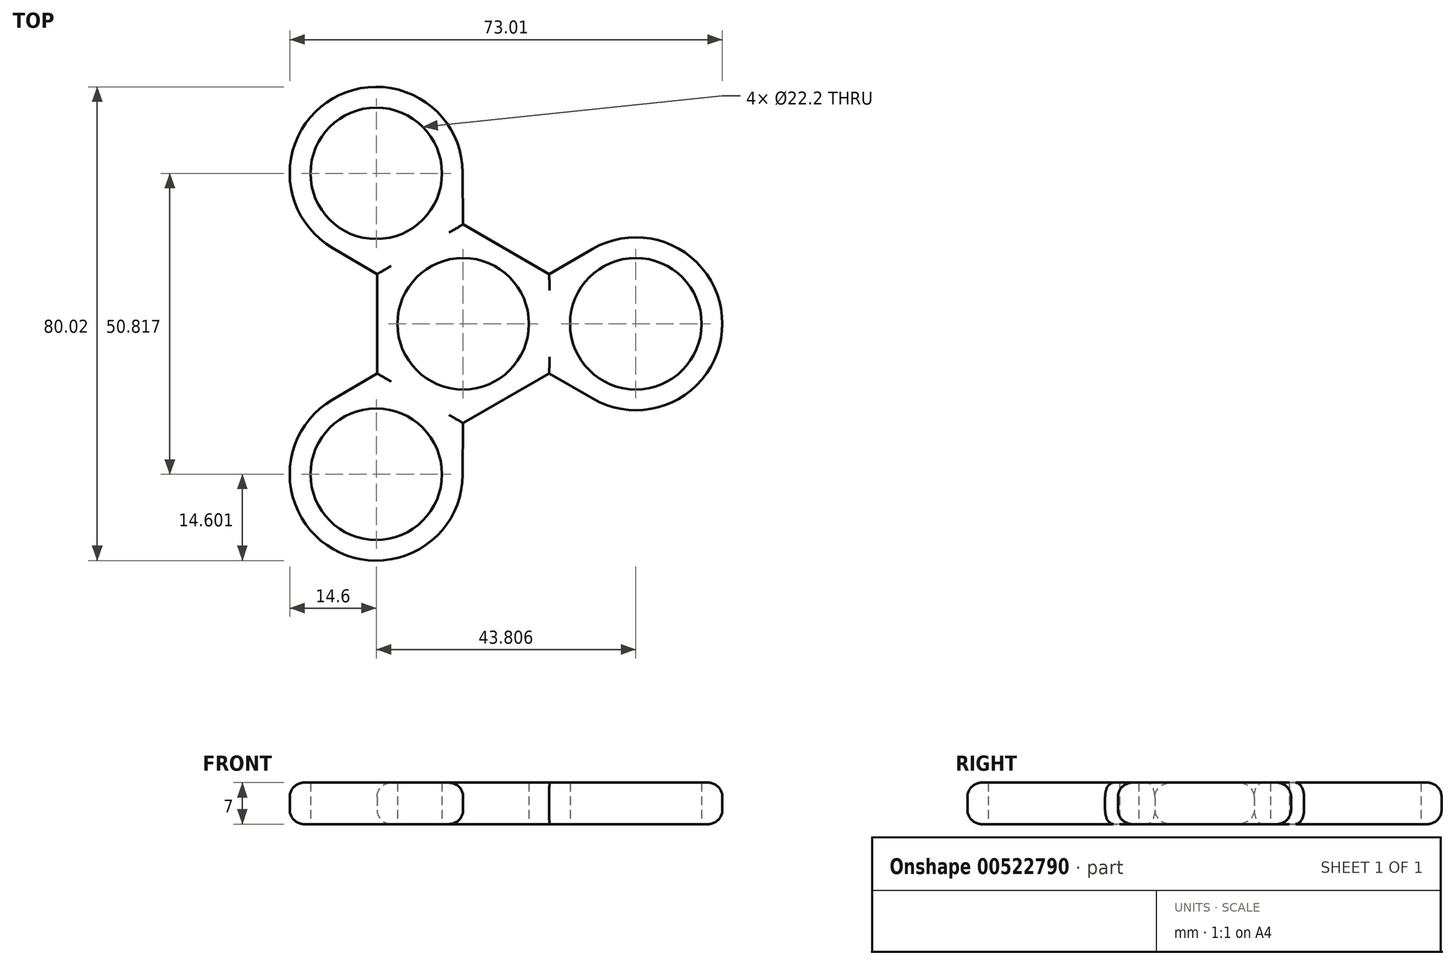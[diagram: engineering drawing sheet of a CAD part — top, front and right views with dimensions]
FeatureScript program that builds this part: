
annotation { "Feature Type Name" : "Feature", "Feature Type Description" : "" }
export const myFeature = defineFeature(function(context is Context, id is Id, definition is map)
    precondition{}
    {
        {
            var Q0;
            Q0=qCreatedBy(makeId("Top.planeOp"),FACE);
            var sketch = newSketch(context, id + "F0", { "sketchPlane" : qUnion([Q0])});
            skCircle(sketch, "E0", {"center": v(0, 0) * mm, "radius": 11.1 * mm});
            skCircle(sketch, "E1.cCircle", {"center": v(0, 0) * mm, "radius": 14.54 * mm, "construction": true});
            skLineSegment(sketch, "E1.0", {"start": v(14.54, 8.4) * mm, "end": v(14.54, -8.4) * mm});
            skLineSegment(sketch, "E1.1", {"start": v(14.54, -8.4) * mm, "end": v(0, -16.79) * mm});
            skLineSegment(sketch, "E1.2", {"start": v(0, -16.79) * mm, "end": v(-14.54, -8.4) * mm});
            skLineSegment(sketch, "E1.3", {"start": v(-14.54, -8.4) * mm, "end": v(-14.54, 8.4) * mm});
            skLineSegment(sketch, "E1.4", {"start": v(-14.54, 8.4) * mm, "end": v(0, 16.79) * mm});
            skLineSegment(sketch, "E1.5", {"start": v(0, 16.79) * mm, "end": v(14.54, 8.4) * mm});
            skPoint(sketch, "E1.0.midPoint", {"position": v(14.54, 0) * mm});
            skCircle(sketch, "E2", {"center": v(-14.67, 25.4) * mm, "radius": 11.1 * mm});
            skLineSegment(sketch, "E3", {"start": v(-14.54, 8.4) * mm, "end": v(-14.54, 14.3) * mm});
            skLineSegment(sketch, "E4", {"start": v(0, 16.79) * mm, "end": v(-5.12, 19.74) * mm});
            skCircle(sketch, "E5", {"center": v(29.14, 0) * mm, "radius": 11.1 * mm});
            skLineSegment(sketch, "E6", {"start": v(14.54, 8.4) * mm, "end": v(19.5, 5.52) * mm});
            skLineSegment(sketch, "E7", {"start": v(14.54, -8.4) * mm, "end": v(19.5, -5.52) * mm});
            skCircle(sketch, "E8.0", {"center": v(29.14, 0) * mm, "radius": 14.6 * mm});
            skCircle(sketch, "E9.0", {"center": v(-14.67, 25.4) * mm, "radius": 14.6 * mm});
            skCircle(sketch, "E10", {"center": v(-14.67, -25.4) * mm, "radius": 11.1 * mm});
            skPoint(sketch, "E11.endSnap0", {"position": v(-7.27, -12.59) * mm});
            skLineSegment(sketch, "E12", {"start": v(-14.54, -8.4) * mm, "end": v(-14.54, -14.3) * mm});
            skLineSegment(sketch, "E13", {"start": v(0, -16.79) * mm, "end": v(-5.12, -19.74) * mm});
            skCircle(sketch, "E14.0", {"center": v(-14.67, -25.4) * mm, "radius": 14.6 * mm});
            skLineSegment(sketch, "E15", {"start": v(-14.54, 8.4) * mm, "end": v(-22.07, 12.82) * mm});
            skLineSegment(sketch, "E16", {"start": v(0, 16.79) * mm, "end": v(-0.07, 25.53) * mm});
            skLineSegment(sketch, "E17", {"start": v(14.54, 8.4) * mm, "end": v(21.79, 12.62) * mm});
            skLineSegment(sketch, "E18", {"start": v(14.54, -8.4) * mm, "end": v(21.79, -12.62) * mm});
            skLineSegment(sketch, "E19", {"start": v(-14.54, -8.4) * mm, "end": v(-22.07, -12.82) * mm});
            skLineSegment(sketch, "E20", {"start": v(0, -16.79) * mm, "end": v(-0.07, -25.53) * mm});
            skSolve(sketch);
        }
        {
            var Q0;
            {var subQ1=sQuery(id+"F0.wireOp",EDGE,"E2");var subQ7=sQuery(id+"F0.wireOp",EDGE,"E3");var subQ8=makeQuery(id+"F0.imprint","INTERSECT",VERTEX,{"derivedFrom":[subQ1,subQ7]});Q0=makeQuery(id+"F0.imprint","IMPRINT",FACE,{"disambiguationData":[TD([[makeQuery(id+"F0.imprint","IMPRINT",EDGE,{"disambiguationData":[TD([[subQ8,1.0]])],"derivedFrom":subQ1}),-1.0]])]});}
            var Q1;
            {var subQ0=sQuery(id+"F0.wireOp",EDGE,"E16");Q1=makeQuery(id+"F0.imprint","IMPRINT",FACE,{"disambiguationData":[TD([[makeQuery(id+"F0.imprint","IMPRINT",EDGE,{"derivedFrom":subQ0}),1.0]])]});}
            var Q2;
            {var subQ0=sQuery(id+"F0.wireOp",EDGE,"E15");Q2=makeQuery(id+"F0.imprint","IMPRINT",FACE,{"disambiguationData":[TD([[makeQuery(id+"F0.imprint","IMPRINT",EDGE,{"derivedFrom":subQ0}),-1.0]])]});}
            var Q3;
            {var subQ0=sQuery(id+"F0.wireOp",EDGE,"E3");var subQ1=sQuery(id+"F0.wireOp",EDGE,"E2");var subQ2=makeQuery(id+"F0.imprint","INTERSECT",VERTEX,{"derivedFrom":[subQ1,subQ0]});Q3=makeQuery(id+"F0.imprint","IMPRINT",FACE,{"disambiguationData":[TD([[makeQuery(id+"F0.imprint","IMPRINT",EDGE,{"disambiguationData":[TD([[subQ2,-1.0]])],"derivedFrom":subQ1}),-1.0]])]});}
            var Q4;
            {var subQ0=sQuery(id+"F0.wireOp",EDGE,"E1.4");Q4=makeQuery(id+"F0.imprint","IMPRINT",FACE,{"disambiguationData":[TD([[makeQuery(id+"F0.imprint","IMPRINT",EDGE,{"derivedFrom":subQ0}),1.0]])]});}
            var Q5;
            Q5=makeQuery(id+"F0.imprint","IMPRINT",FACE,{"disambiguationData":[TD([[makeQuery(id+"F0.imprint","IMPRINT",EDGE,{"derivedFrom":sQuery(id+"F0.wireOp",EDGE,"E0")}),-1.0]])]});
            var Q6;
            {var subQ1=sQuery(id+"F0.wireOp",EDGE,"E5");var subQ5=sQuery(id+"F0.wireOp",EDGE,"E6");var subQ6=makeQuery(id+"F0.imprint","INTERSECT",VERTEX,{"derivedFrom":[subQ1,subQ5]});Q6=makeQuery(id+"F0.imprint","IMPRINT",FACE,{"disambiguationData":[TD([[makeQuery(id+"F0.imprint","IMPRINT",EDGE,{"disambiguationData":[TD([[subQ6,1.0]])],"derivedFrom":subQ1}),-1.0]])]});}
            var Q7;
            {var subQ0=sQuery(id+"F0.wireOp",EDGE,"E17");Q7=makeQuery(id+"F0.imprint","IMPRINT",FACE,{"disambiguationData":[TD([[makeQuery(id+"F0.imprint","IMPRINT",EDGE,{"derivedFrom":subQ0}),-1.0]])]});}
            var Q8;
            {var subQ0=sQuery(id+"F0.wireOp",EDGE,"E1.0");Q8=makeQuery(id+"F0.imprint","IMPRINT",FACE,{"disambiguationData":[TD([[makeQuery(id+"F0.imprint","IMPRINT",EDGE,{"derivedFrom":subQ0}),1.0]])]});}
            var Q9;
            {var subQ0=sQuery(id+"F0.wireOp",EDGE,"E6");var subQ1=sQuery(id+"F0.wireOp",EDGE,"E5");var subQ2=makeQuery(id+"F0.imprint","INTERSECT",VERTEX,{"derivedFrom":[subQ1,subQ0]});Q9=makeQuery(id+"F0.imprint","IMPRINT",FACE,{"disambiguationData":[TD([[makeQuery(id+"F0.imprint","IMPRINT",EDGE,{"disambiguationData":[TD([[subQ2,-1.0]])],"derivedFrom":subQ1}),-1.0]])]});}
            var Q10;
            {var subQ0=sQuery(id+"F0.wireOp",EDGE,"E18");Q10=makeQuery(id+"F0.imprint","IMPRINT",FACE,{"disambiguationData":[TD([[makeQuery(id+"F0.imprint","IMPRINT",EDGE,{"derivedFrom":subQ0}),1.0]])]});}
            var Q11;
            {var subQ0=sQuery(id+"F0.wireOp",EDGE,"E12");var subQ1=sQuery(id+"F0.wireOp",EDGE,"E10");var subQ2=makeQuery(id+"F0.imprint","INTERSECT",VERTEX,{"derivedFrom":[subQ1,subQ0]});Q11=makeQuery(id+"F0.imprint","IMPRINT",FACE,{"disambiguationData":[TD([[makeQuery(id+"F0.imprint","IMPRINT",EDGE,{"disambiguationData":[TD([[subQ2,1.0]])],"derivedFrom":subQ1}),-1.0]])]});}
            var Q12;
            {var subQ2=sQuery(id+"F0.wireOp",EDGE,"E12");var subQ5=sQuery(id+"F0.wireOp",EDGE,"E10");var subQ8=makeQuery(id+"F0.imprint","INTERSECT",VERTEX,{"derivedFrom":[subQ5,subQ2]});Q12=makeQuery(id+"F0.imprint","IMPRINT",FACE,{"disambiguationData":[TD([[makeQuery(id+"F0.imprint","IMPRINT",EDGE,{"disambiguationData":[TD([[subQ8,-1.0]])],"derivedFrom":subQ5}),-1.0]])]});}
            var Q13;
            {var subQ0=sQuery(id+"F0.wireOp",EDGE,"E19");Q13=makeQuery(id+"F0.imprint","IMPRINT",FACE,{"disambiguationData":[TD([[makeQuery(id+"F0.imprint","IMPRINT",EDGE,{"derivedFrom":subQ0}),1.0]])]});}
            var Q14;
            {var subQ0=sQuery(id+"F0.wireOp",EDGE,"E1.2");Q14=makeQuery(id+"F0.imprint","IMPRINT",FACE,{"disambiguationData":[TD([[makeQuery(id+"F0.imprint","IMPRINT",EDGE,{"derivedFrom":subQ0}),1.0]])]});}
            var Q15;
            {var subQ0=sQuery(id+"F0.wireOp",EDGE,"E20");Q15=makeQuery(id+"F0.imprint","IMPRINT",FACE,{"disambiguationData":[TD([[makeQuery(id+"F0.imprint","IMPRINT",EDGE,{"derivedFrom":subQ0}),-1.0]])]});}
            extrude(context, id + "F1", {"entities" : qUnion([Q0, Q1, Q2, Q3, Q4, Q5, Q6, Q7, Q8, Q9, Q10, Q11, Q12, Q13, Q14, Q15]), "depth" : 7 * mm, "offsetDistance" : 25 * mm});
        }
        {
            var Q0;
            Q0=makeQuery(id+"F1.opExtrude","CAP_EDGE",EDGE,{"disambiguationData":[OSD([sQuery(id+"F0.wireOp",EDGE,"E19")])],"isStart":true});
            var Q1;
            Q1=makeQuery(id+"F1.opExtrude","CAP_EDGE",EDGE,{"disambiguationData":[OSD([sQuery(id+"F0.wireOp",EDGE,"E15")])],"isStart":true});
            var Q2;
            Q2=makeQuery(id+"F1.opExtrude","CAP_EDGE",EDGE,{"disambiguationData":[OSD([sQuery(id+"F0.wireOp",EDGE,"E14.0")])],"isStart":false});
            var Q3;
            Q3=makeQuery(id+"F1.opExtrude","SWEPT_FACE",FACE,{"disambiguationData":[OSD([sQuery(id+"F0.wireOp",EDGE,"E9.0")])]});
            var Q4;
            Q4=makeQuery(id+"F1.opExtrude","CAP_EDGE",EDGE,{"disambiguationData":[OSD([sQuery(id+"F0.wireOp",EDGE,"E17")])],"isStart":false});
            var Q5;
            Q5=makeQuery(id+"F1.opExtrude","CAP_EDGE",EDGE,{"disambiguationData":[OSD([sQuery(id+"F0.wireOp",EDGE,"E17")])],"isStart":true});
            var Q6;
            Q6=makeQuery(id+"F1.opExtrude","CAP_EDGE",EDGE,{"disambiguationData":[OSD([sQuery(id+"F0.wireOp",EDGE,"E1.3")])],"isStart":true});
            var Q7;
            Q7=makeQuery(id+"F1.opExtrude","CAP_EDGE",EDGE,{"disambiguationData":[OSD([sQuery(id+"F0.wireOp",EDGE,"E1.5")])],"isStart":false});
            var Q8;
            Q8=makeQuery(id+"F1.opExtrude","CAP_EDGE",EDGE,{"disambiguationData":[OSD([sQuery(id+"F0.wireOp",EDGE,"E1.5")])],"isStart":true});
            var Q9;
            Q9=makeQuery(id+"F1.opExtrude","CAP_EDGE",EDGE,{"disambiguationData":[OSD([sQuery(id+"F0.wireOp",EDGE,"E1.1")])],"isStart":true});
            var Q10;
            Q10=makeQuery(id+"F1.opExtrude","CAP_EDGE",EDGE,{"disambiguationData":[OSD([sQuery(id+"F0.wireOp",EDGE,"E1.3")])],"isStart":false});
            var Q11;
            Q11=makeQuery(id+"F1.opExtrude","CAP_EDGE",EDGE,{"disambiguationData":[OSD([sQuery(id+"F0.wireOp",EDGE,"E1.1")])],"isStart":false});
            fillet(context, id + "F2", {"entities" : qUnion([Q0, Q1, Q2, Q3, Q4, Q5, Q6, Q7, Q8, Q9, Q10, Q11]), "radius" : 2.4 * mm, "tangentPropagation" : true, "allowEdgeOverflow" : false});
        }
    });
